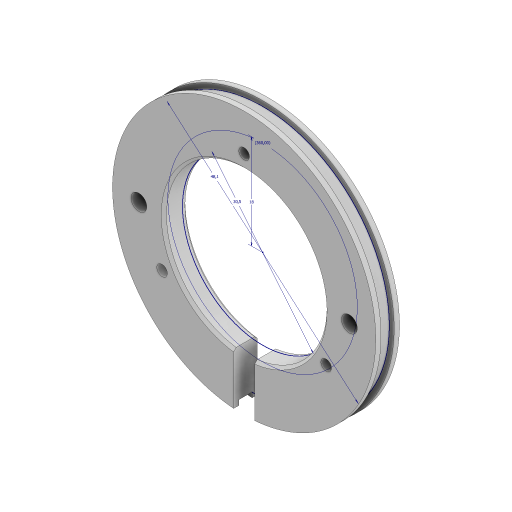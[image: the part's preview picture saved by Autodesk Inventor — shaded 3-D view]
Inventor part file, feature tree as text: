
AUTODESK INVENTOR PART (.ipt)
format: ipt  version: 2023 (Build 270158000, 158)  size: 187,904 bytes
history: native  units: mm
features: sketch x5, extrude x4, hole x2, chamfer x1
ambient origin geometry x8: Origin, YZ Plane, XZ Plane, XY Plane, X Axis, Y Axis, Z Axis, Center Point
bodies: Solid1 (feature_tree)
feature tree (12):
  sketch  "Sketch1"  dims[d0=30.5mm d1=48.1mm]
  extrude  "Extrusion1"  Depth=48.1mm
  hole  "Hole1"  [1 undecoded]
  extrude  "Extrusion2"  Depth=50.0mm
  extrude  "Extrusion3"  Depth=1.0mm TaperAngle=0.0deg
  extrude  "Extrusion4"  Depth=1.0mm
  hole  "Hole2"  [1 undecoded]
  chamfer  "Chamfer1"  Distance=20.0mm
  sketch  "Sketch2"  dims[d2=18.0mm d3=30.0mm d5=360.0deg]
  sketch  "Sketch3"  dims[d7=2.5mm d8=0.0mm]
  sketch  "Sketch4"  dims[d9=2.0mm d10=6.0mm d11=4.0mm d12=2.0mm d13=90.0deg d14=8.0mm d15=20.594885mm d16=50.0mm]
  sketch  "Sketch5"  dims[d17=1.0mm d18=0.0mm d19=1.0mm d20=0.0mm d21=50.0mm d22=4.0mm d23=20.0mm d24=0.0mm d25=0.0mm d26=3.0mm d27=6.0mm d28=4.0mm d29=2.0mm d30=90.0deg d31=8.0mm d32=20.594885mm d33=0.0mm d34=0.5mm d35=2.0mm d36=45.0deg]
note: 2 required parameter values undecoded (feature->parameter linkage not recoverable at this tier; creation-order binding heuristic only, values carry confidence <= 0.55)
